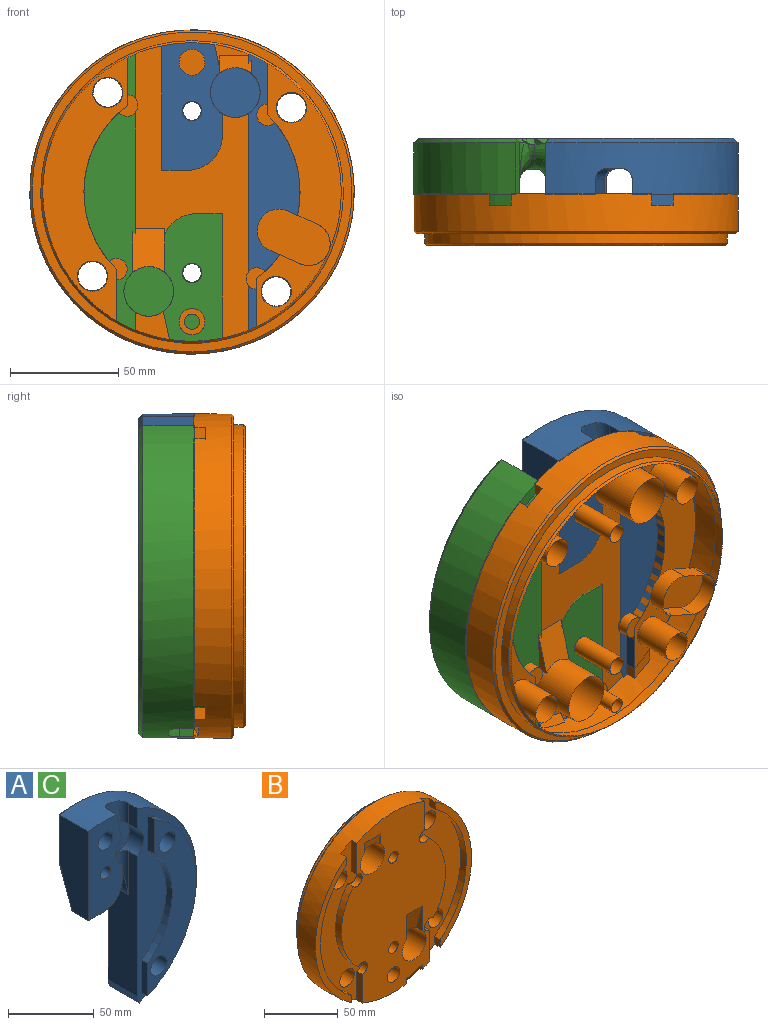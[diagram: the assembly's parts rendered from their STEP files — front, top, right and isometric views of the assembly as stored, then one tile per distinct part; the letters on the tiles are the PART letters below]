
ASSEMBLY  parts=3 mates=1
PART A: 53 faces, bbox 92.2x44.9x145.8 mm
  f0: plane 100.54x24mm, normal (-1,0,0), area 1882.7mm2, adj f3,f10,f11,f22,f41,f45
  f1: plane 140.6x85.18mm, normal (0,1,0), area 5656.2mm2, adj f35,f37,f39,f40,f42,f43,f45,f47
  f2: cylinder r=75mm len=144.67mm, axis (0,1,0), area 5112.4mm2, adj f3,f4,f8,f18,f19,f20,f29,f30
  f3: plane 140.02x49mm, normal (0,-1,0), area 2542.8mm2, adj f0,f2,f10,f12,f13,f14,f15,f20
  f4: plane 63.68x24mm, normal (-1,0,0), area 1377.5mm2, adj f2,f8,f9,f42,f44
  f5: cylinder r=6.75mm len=19mm, axis (0,-1,0), area 805.8mm2, adj f16,f38
  f6: cylinder r=6.75mm len=19mm, axis (0,-1,0), area 805.8mm2, adj f16,f36
  f7: cylinder r=4.25mm len=17mm, axis (0,-1,0), area 454mm2, adj f8,f34
  f8: plane 65x28mm, normal (0,-1,0), area 1454.9mm2, adj f2,f4,f7,f9,f17,f21,f24,f30
  f9: plane 19.35x16.02mm, normal (0,0,-1), area 201.1mm2, adj f4,f8,f24,f25,f46
  f10: cylinder r=11.5mm len=22.32mm, axis (0,-1,0), area 294.7mm2, adj f0,f3,f18,f19,f20,f22,f29
  f11: cylinder r=5mm len=17mm, axis (0,1,0), area 40.1mm2, adj f0,f28,f47
  f12: plane 23.25x5mm, normal (-1,0,0), area 116.2mm2, adj f3,f13,f15,f16
  f13: cylinder r=70mm len=123.87mm, axis (0,1,0), area 761.3mm2, adj f3,f12,f14,f16
  f14: plane 24.91x5mm, normal (-1,0,0), area 124.6mm2, adj f3,f13,f15,f16
  f15: cylinder r=50mm len=75.71mm, axis (0,1,0), area 430.7mm2, adj f3,f12,f14,f16
  f16: plane 123.87x40mm, normal (0,-1,0), area 2104.6mm2, adj f5,f6,f12,f13,f14,f15
  f17: cylinder r=11.5mm len=22.75mm, axis (0,-1,0), area 297.3mm2, adj f8,f18,f21,f23,f30,f31
  f18: plane 47.75x23mm, normal (0,-1,0), area 541.6mm2, adj f2,f10,f17,f22,f23,f27,f29,f31
  f19: cylinder r=5mm len=16mm, axis (0,0,1), area 88.1mm2, adj f2,f10,f20,f29
  f20: plane 14.54x7mm, normal (-1,0,0), area 101.8mm2, adj f2,f3,f10,f19
  f21: plane 10.19x7mm, normal (1,0,0), area 71.3mm2, adj f8,f17,f23,f24
  f22: cylinder r=5mm len=31.19mm, axis (0,0,1), area 134.4mm2, adj f0,f10,f18,f27,f28
  f23: cylinder r=5mm len=10.31mm, axis (0,0,1), area 73.7mm2, adj f17,f18,f21,f25,f26
  f24: cylinder r=16mm len=16mm, axis (0,-1,0), area 175.9mm2, adj f8,f9,f21,f25
  f25: torus R=21mm, axis (0,0,1), area 288.2mm2, adj f9,f23,f24,f26,f48
  f26: bspline ~16.84x14.71mm, area 84.4mm2, adj f23,f25,f27,f50,f52
  f27: bspline ~16.35x14.48mm, area 57mm2, adj f18,f22,f26,f28,f51
  f28: bspline ~19.09x19mm, area 154.1mm2, adj f11,f22,f27,f49
  f29: plane 16.64x4.58mm, normal (-0.58,0.81,-0.12), area 10.1mm2, adj f2,f10,f18,f19
  f30: plane 19.12x7mm, normal (0.98,0,0.21), area 137mm2, adj f2,f8,f17,f31
  f31: bspline ~19.12x9.14mm, area 140.9mm2, adj f2,f17,f18,f30
  f32: cylinder r=6mm len=15mm, axis (0,-1,0), area 565.5mm2, adj f8,f33
  f33: plane 12x12mm, normal (0,-1,0), area 113.1mm2, adj f32
  f34: plane 14x14mm, normal (0,1,0), area 97.2mm2, adj f7,f35
  f35: cylinder r=7mm len=14mm, axis (0,1,0), area 395.8mm2, adj f1,f34
  f36: plane 20x20mm, normal (0,1,0), area 171mm2, adj f6,f37
  f37: cylinder r=10mm len=20mm, axis (0,1,0), area 754mm2, adj f1,f36
  f38: plane 20x20mm, normal (0,1,0), area 171mm2, adj f5,f39
  f39: cylinder r=10mm len=20mm, axis (0,1,0), area 754mm2, adj f1,f38
  f40: plane 27.38x27.05mm, normal (-0.33,0.89,-0.33), area 415.6mm2, adj f1,f42,f44,f46,f48,f50,f52
  f41: plane 25.35x5.32mm, normal (-0.95,0,-0.32), area 138.3mm2, adj f0,f2,f3,f43,f45
  f42: plane 36.83x2.02mm, normal (-0.71,0.71,0), area 99.5mm2, adj f1,f4,f40,f43,f44
  f43: cone r=75mm half-angle=45deg, axis (0,-1,0), area 614.5mm2, adj f1,f2,f41,f42,f45
  f44: plane 28.69x11.87mm, normal (-0.81,0.55,-0.2), area 67.1mm2, adj f4,f40,f42,f46
  f45: plane 73.39x2mm, normal (-0.71,0.71,0), area 203.3mm2, adj f0,f1,f41,f43,f47
  f46: plane 16.02x7.65mm, normal (-0.2,0.55,-0.81), area 37.2mm2, adj f9,f40,f44,f48
  f47: cone r=7mm half-angle=45deg, axis (0,1,0), area 16mm2, adj f1,f11,f45,f49
  f48: bspline ~10.32x5.39mm, area 25.9mm2, adj f25,f40,f46,f50
  f49: bspline ~2.82x2.79mm, area 5.9mm2, adj f1,f28,f47,f51
  f50: bspline ~5.97x4.08mm, area 5.9mm2, adj f26,f40,f48,f52
  f51: bspline ~4.28x2.6mm, area 12.4mm2, adj f1,f27,f49,f52
  f52: bspline ~6.52x2.57mm, area 17.5mm2, adj f1,f26,f40,f50,f51
PART B: 52 faces, bbox 150.5x24.5x150.5 mm
  f0: plane 150x100mm, normal (0,-1,0), area 9581.3mm2, adj f1,f2,f3,f12,f13,f14,f15,f16
  f1: cylinder r=11.5mm len=24mm, axis (0,-1,0), area 1715.6mm2, adj f0,f4,f47,f48,f49
  f2: cylinder r=75mm len=150mm, axis (0,1,0), area 7957.1mm2, adj f0,f6,f7,f11,f12,f16,f17,f18
  f3: cylinder r=11.5mm len=24mm, axis (0,-1,0), area 1653.4mm2, adj f0,f4,f41,f42,f43
  f4: plane 138x138mm, normal (0,1,0), area 12730.5mm2, adj f1,f3,f5,f30,f31,f32,f33,f34
  f5: cylinder r=3.5mm len=12mm, axis (0,-1,0), area 263.9mm2, adj f4,f28
  f6: plane 123.44x35mm, normal (0,-1,0), area 684.2mm2, adj f2,f10,f11,f17
  f7: plane 123.44x35mm, normal (0,-1,0), area 684.2mm2, adj f2,f23,f24,f25
  f8: plane 148x148mm, normal (0,1,0), area 1809.6mm2, adj f9,f51
  f9: cylinder r=70mm len=140mm, axis (0,-1,0), area 1979.2mm2, adj f8,f50
  f10: cylinder r=70mm len=111.06mm, axis (0,-1,0), area 706.5mm2, adj f6,f11,f17,f18
  f11: plane 6x5.5mm, normal (-1,0,0), area 33mm2, adj f2,f6,f10,f18
  f12: plane 23.74x5.5mm, normal (1,0,0), area 130.6mm2, adj f0,f2,f13,f18
  f13: cylinder r=5mm len=10mm, axis (0,-1,0), area 110.5mm2, adj f0,f12,f14,f18
  f14: cylinder r=50mm len=68.84mm, axis (0,-1,0), area 418.7mm2, adj f0,f13,f15,f18
  f15: cylinder r=5mm len=10mm, axis (0,-1,0), area 106.9mm2, adj f0,f14,f16,f18
  f16: plane 25.63x5.5mm, normal (1,0,0), area 140.9mm2, adj f0,f2,f15,f18
  f17: plane 6.38x5.5mm, normal (-1,0,0), area 35.1mm2, adj f2,f6,f10,f18
  f18: plane 135.07x45mm, normal (0,-1,0), area 2299.6mm2, adj f2,f10,f11,f12,f13,f14,f15,f16
  f19: cylinder r=5mm len=10mm, axis (0,-1,0), area 110.5mm2, adj f0,f20,f26,f27
  f20: cylinder r=50mm len=68.84mm, axis (0,-1,0), area 418.7mm2, adj f0,f19,f21,f27
  f21: cylinder r=5mm len=10mm, axis (0,-1,0), area 106.9mm2, adj f0,f20,f22,f27
  f22: plane 25.63x5.5mm, normal (-1,0,0), area 140.9mm2, adj f0,f2,f21,f27
  f23: plane 6.38x5.5mm, normal (1,0,0), area 35.1mm2, adj f2,f7,f24,f27
  f24: cylinder r=70mm len=111.06mm, axis (0,-1,0), area 706.5mm2, adj f7,f23,f25,f27
  f25: plane 6x5.5mm, normal (1,0,0), area 33mm2, adj f2,f7,f24,f27
  f26: plane 23.74x5.5mm, normal (-1,0,0), area 130.6mm2, adj f0,f2,f19,f27
  f27: plane 135.07x45mm, normal (0,-1,0), area 2299.6mm2, adj f2,f19,f20,f21,f22,f23,f24,f25
  f28: plane 12x12mm, normal (0,-1,0), area 74.6mm2, adj f5,f29
  f29: cylinder r=6mm len=12mm, axis (0,-1,0), area 452.4mm2, adj f0,f28
  f30: cylinder r=7mm len=18.5mm, axis (0,-1,0), area 813.7mm2, adj f4,f27
  f31: cylinder r=7mm len=18.5mm, axis (0,-1,0), area 813.7mm2, adj f4,f27
  f32: cylinder r=7mm len=18.5mm, axis (0,-1,0), area 813.7mm2, adj f4,f18
  f33: cylinder r=7mm len=18.5mm, axis (0,-1,0), area 813.7mm2, adj f4,f18
  f34: cylinder r=4.5mm len=24mm, axis (0,-1,0), area 678.6mm2, adj f0,f4
  f35: cylinder r=4.5mm len=24mm, axis (0,-1,0), area 678.6mm2, adj f0,f4
  f36: cylinder r=10mm len=19.14mm, axis (0,1,0), area 251.3mm2, adj f4,f37,f39,f40
  f37: plane 13.7x8mm, normal (-0.41,0,0.91), area 120mm2, adj f4,f36,f38,f40
  f38: cylinder r=10mm len=19.14mm, axis (0,1,0), area 251.3mm2, adj f4,f37,f39,f40
  f39: plane 13.7x8mm, normal (0.41,0,-0.91), area 120mm2, adj f4,f36,f38,f40
  f40: plane 33.7x26.1mm, normal (0,1,0), area 614.2mm2, adj f36,f37,f38,f39
  f41: plane 20.28x5.43mm, normal (1,0,0), area 55.1mm2, adj f0,f3,f43
  f42: plane 20.28x5.43mm, normal (-1,0,0), area 55.1mm2, adj f0,f3,f43
  f43: plane 20.28x15mm, normal (0,-0.97,-0.26), area 285.4mm2, adj f0,f3,f41,f42
  f44: cone r=0mm half-angle=74.4deg, axis (-0.96,0,-0.27), area 4.7mm2, adj f0,f2,f46
  f45: cone r=0mm half-angle=74.4deg, axis (-0.96,0,-0.27), area 4.7mm2, adj f0,f2,f46
  f46: plane 15.63x8.67mm, normal (0.13,-0.87,-0.48), area 74.1mm2, adj f0,f2,f44,f45
  f47: plane 8.28x1.46mm, normal (1,0,0), area 6mm2, adj f0,f1,f49
  f48: plane 8.28x1.46mm, normal (-1,0,0), area 6mm2, adj f0,f1,f49
  f49: plane 15x8.28mm, normal (0,-0.98,-0.17), area 97.1mm2, adj f0,f1,f47,f48
  f50: cone r=69mm half-angle=45deg, axis (0,-1,0), area 617.6mm2, adj f4,f9
  f51: cone r=75mm half-angle=45deg, axis (0,-1,0), area 662mm2, adj f2,f8
PART C: same geometry as A
PLACE A t=(108.89,59.34,-31.79)mm
PLACE B rot(axis=(0,0,-1),180deg) t=(108.89,15.34,-31.79)mm fixed
PLACE C rot(axis=(0,-1,0),180deg) t=(108.89,59.34,-31.79)mm
MATE fastened B.f32 <-> C.f6  axis (0,1,0) through (62.89,28.34,-70.79)mm
